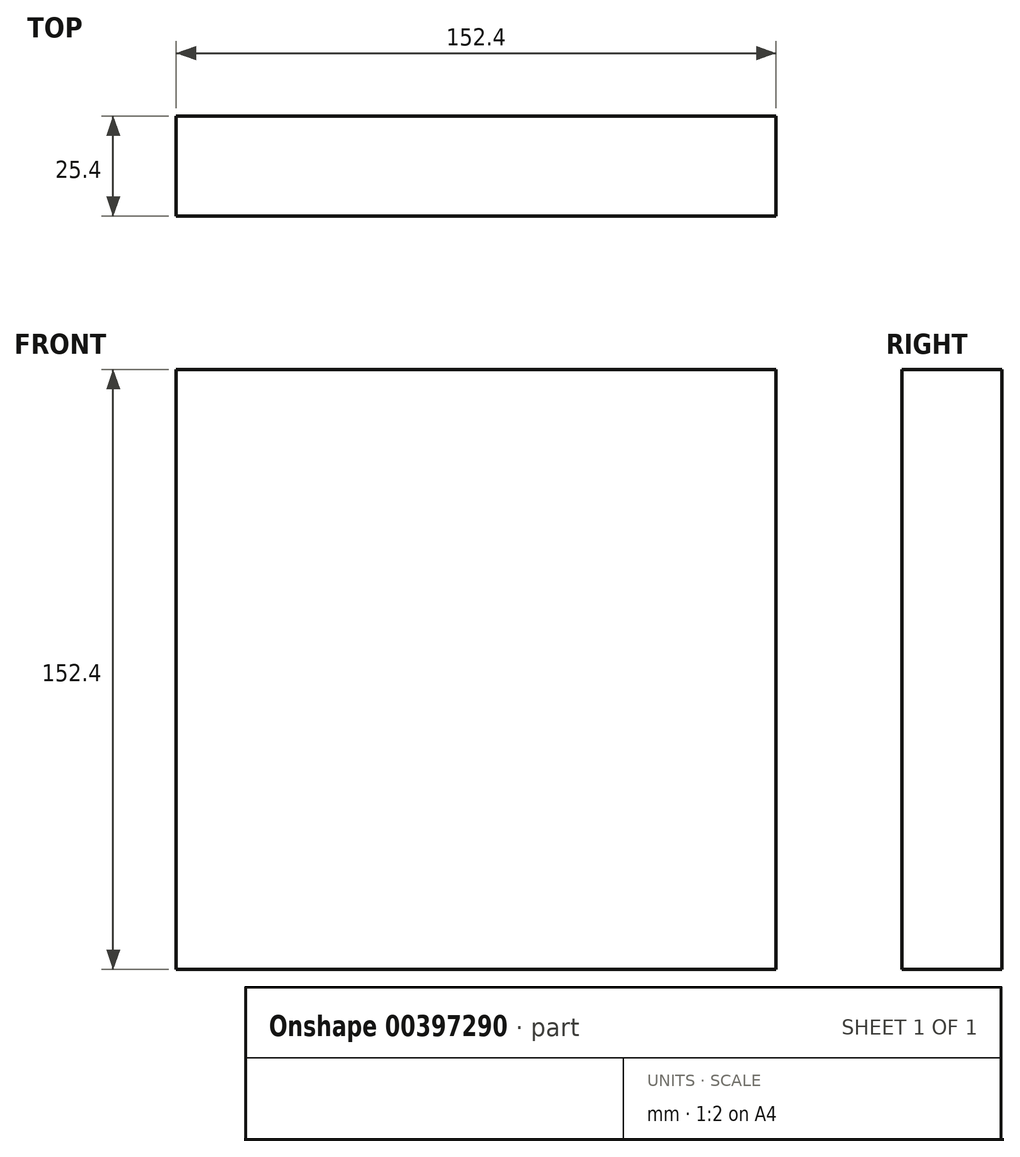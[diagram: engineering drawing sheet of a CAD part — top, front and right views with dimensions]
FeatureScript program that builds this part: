
annotation { "Feature Type Name" : "Feature", "Feature Type Description" : "" }
export const myFeature = defineFeature(function(context is Context, id is Id, definition is map)
    precondition{}
    {
        {
            var Q0;
            Q0=qCreatedBy(makeId("Front.planeOp"),FACE);
            var sketch = newSketch(context, id + "F0", { "sketchPlane" : qUnion([Q0])});
            skLineSegment(sketch, "E0.bottom", {"start": v(-91.13, -82.6) * mm, "end": v(61.27, -82.6) * mm});
            skLineSegment(sketch, "E0.top", {"start": v(-91.13, 69.8) * mm, "end": v(61.27, 69.8) * mm});
            skLineSegment(sketch, "E0.left", {"start": v(-91.13, -82.6) * mm, "end": v(-91.13, 69.8) * mm});
            skLineSegment(sketch, "E0.right", {"start": v(61.27, -82.6) * mm, "end": v(61.27, 69.8) * mm});
            skSolve(sketch);
        }
        {
            var Q0;
            Q0=makeQuery(id+"F0.imprint","IMPRINT",FACE,{"disambiguationData":[TD([[makeQuery(id+"F0.imprint","IMPRINT",EDGE,{"derivedFrom":sQuery(id+"F0.wireOp",EDGE,"E0.bottom")}),1.0]])]});
            extrude(context, id + "F1", {"entities" : qUnion([Q0]), "endBound" : BoundingType.SYMMETRIC, "depth" : 25.4 * mm});
        }
    });
